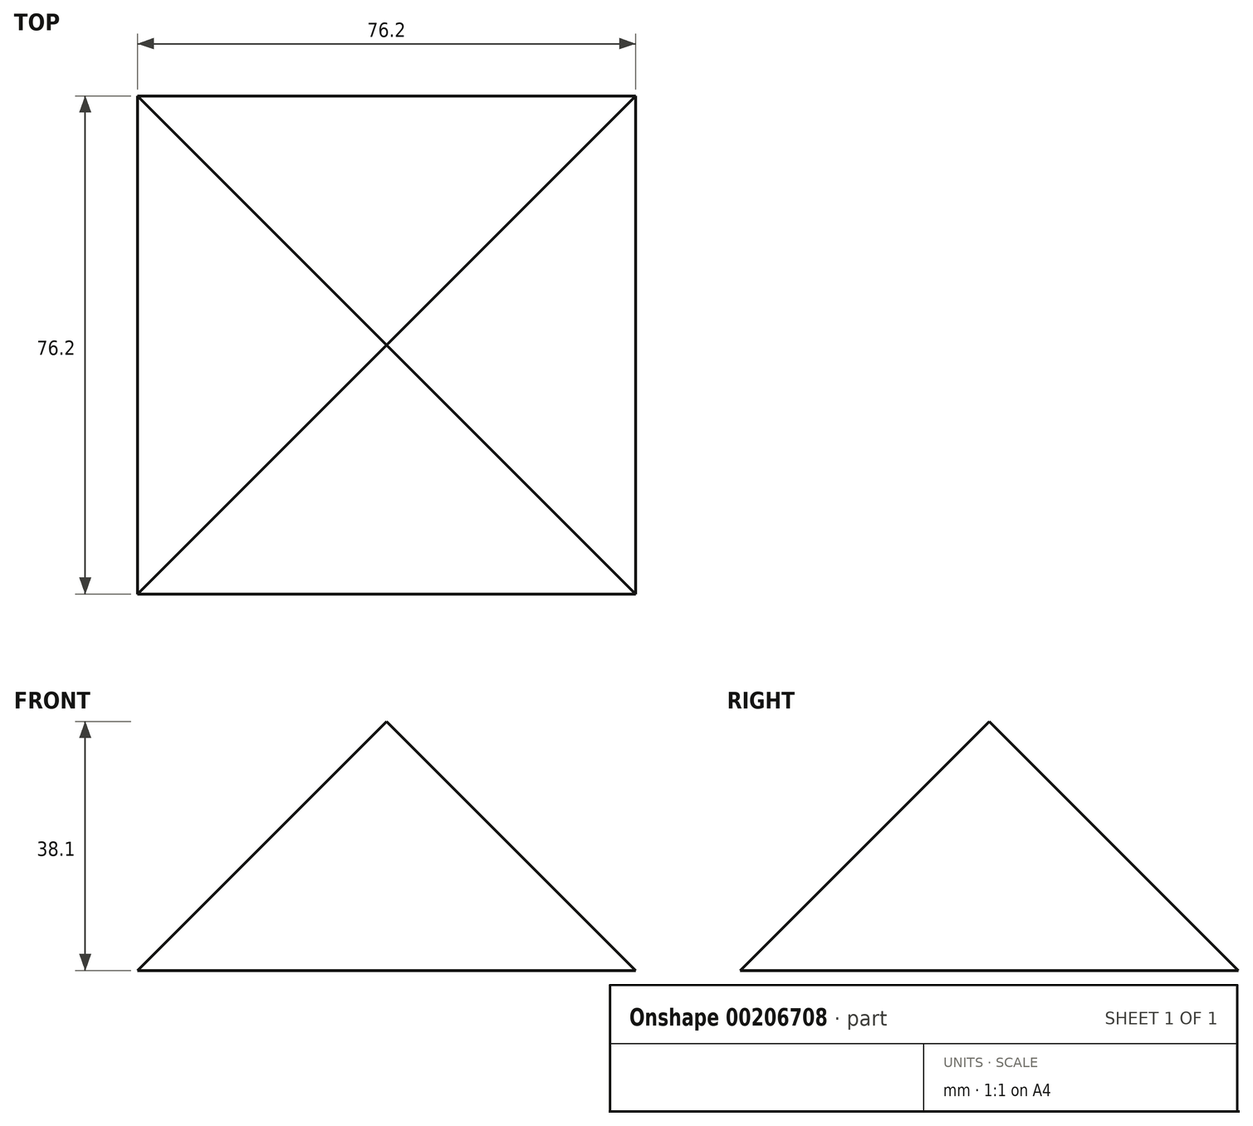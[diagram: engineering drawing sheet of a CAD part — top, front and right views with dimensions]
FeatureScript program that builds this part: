
annotation { "Feature Type Name" : "Feature", "Feature Type Description" : "" }
export const myFeature = defineFeature(function(context is Context, id is Id, definition is map)
    precondition{}
    {
        {
            var Q0;
            Q0=qCreatedBy(makeId("Top.planeOp"), FACE);
            var sketch = newSketch(context, id + "F0", { "sketchPlane" : qUnion([Q0])});
            skLineSegment(sketch, "E0.bottom", {"start": v(38.1, 38.1) * mm, "end": v(-38.1, 38.1) * mm});
            skLineSegment(sketch, "E0.top", {"start": v(38.1, -38.1) * mm, "end": v(-38.1, -38.1) * mm});
            skLineSegment(sketch, "E0.left", {"start": v(38.1, 38.1) * mm, "end": v(38.1, -38.1) * mm});
            skLineSegment(sketch, "E0.right", {"start": v(-38.1, 38.1) * mm, "end": v(-38.1, -38.1) * mm});
            skPoint(sketch, "E0.middle", {"position": v(0, 0) * mm});
            skSolve(sketch);
        }
        {
            var Q0;
            Q0 = qSketchRegion(id + "F0", true);
            extrude(context, id + "F1", {"entities" : qUnion([Q0]), "depth" : 127 * mm, "offsetDistance" : 25.4 * mm, "hasDraft" : true, "draftAngle" : 45 * degree, "draftPullDirection" : true});
        }
    });
